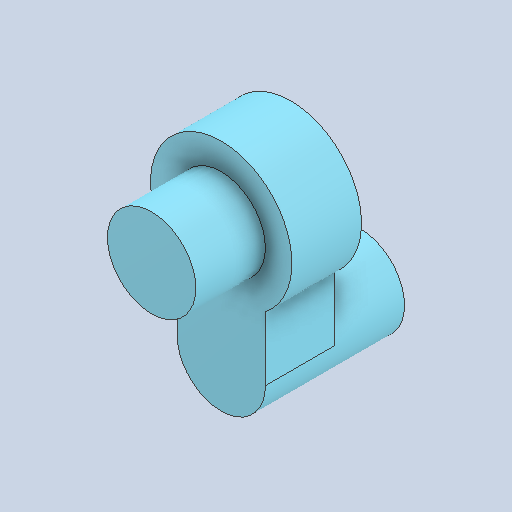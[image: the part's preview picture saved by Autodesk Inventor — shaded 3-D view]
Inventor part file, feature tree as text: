
AUTODESK INVENTOR PART (.ipt)
format: ipt  version: 2022 (Build 260153000, 153)  size: 120,320 bytes
history: native  units: in
note: dims shown in document units (in); Inventor stores cm internally (conversion verified against a paired STEP export)
features: other x3, sketch x2
ambient origin geometry x8: Origin, YZ Plane, XZ Plane, XY Plane, X Axis, Y Axis, Z Axis, Center Point
bodies: Solid1 (feature_tree)
feature tree (5):
  other  "Component37.ipt"
  other  "Solid1::Component37.ipt"
  other  "TaggingFeature1"
  sketch  "Sketch2"  dims[d0=0.3937in]
  sketch  "Sketch3"
